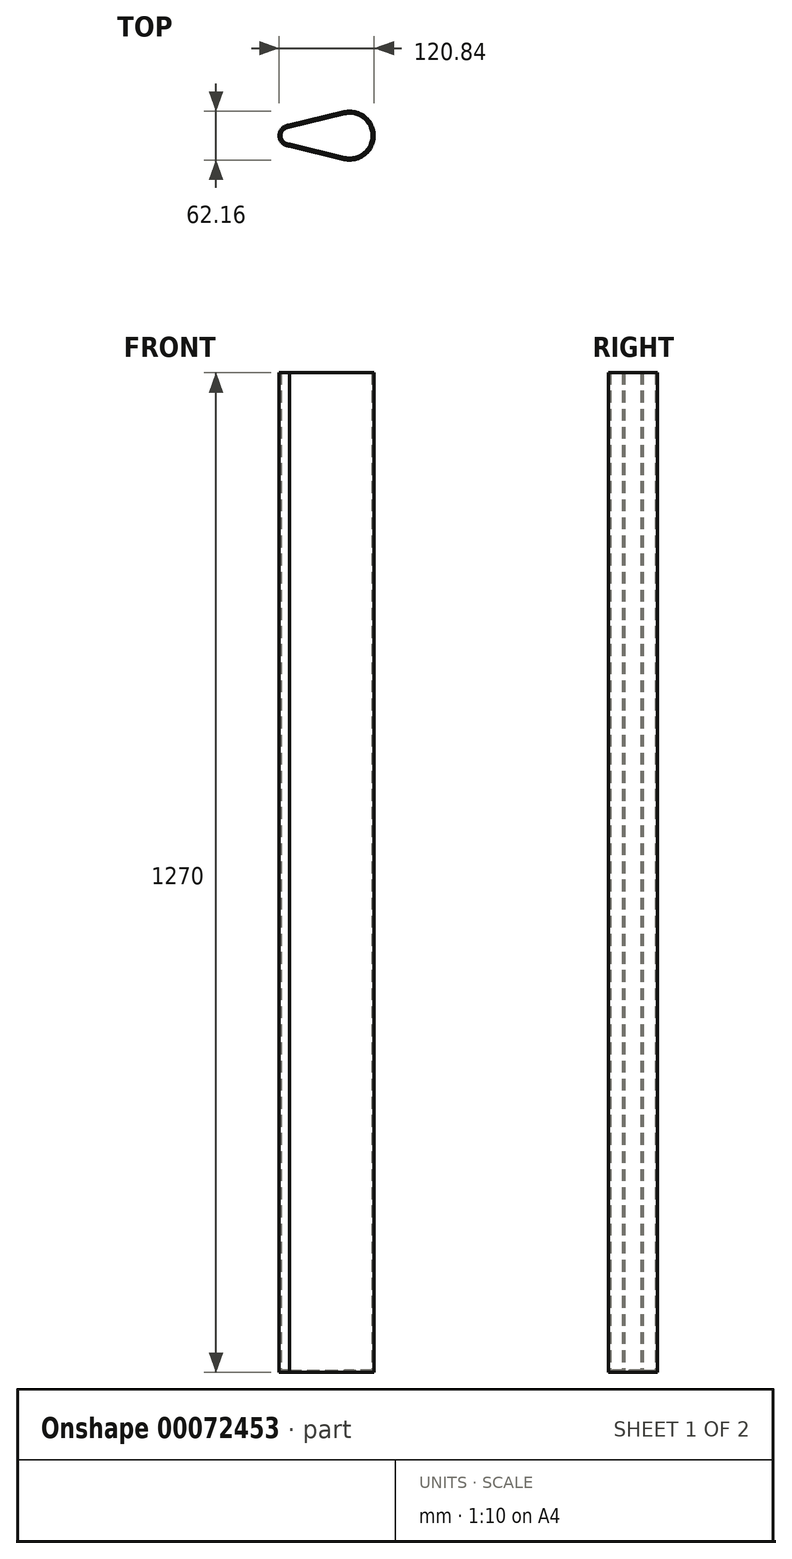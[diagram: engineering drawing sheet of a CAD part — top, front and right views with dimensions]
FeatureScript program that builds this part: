
annotation { "Feature Type Name" : "Feature", "Feature Type Description" : "" }
export const myFeature = defineFeature(function(context is Context, id is Id, definition is map)
    precondition{}
    {
        {
            var Q0;
            Q0=qCreatedBy(makeId("Top.planeOp"),FACE);
            var sketch = newSketch(context, id + "F0", { "sketchPlane" : qUnion([Q0])});
            skArc(sketch, "E0", {"start": v(-7.45, -30.18) * mm, "mid": v(31.08, -0.06) * mm, "end": v(-7.34, 30.2) * mm});
            skArc(sketch, "E1", {"start": v(-77.48, 13.16) * mm, "mid": v(-89.75, -0.6) * mm, "end": v(-76.3, -13.2) * mm});
            skLineSegment(sketch, "E2", {"start": v(-77.48, 13.16) * mm, "end": v(-7.34, 30.2) * mm});
            skLineSegment(sketch, "E3", {"start": v(-76.3, -13.2) * mm, "end": v(-7.45, -30.18) * mm});
            skPoint(sketch, "E4.orphan", {"position": v(0, 31.99) * mm});
            skPoint(sketch, "E5.orphan", {"position": v(0, -32.01) * mm});
            skSolve(sketch);
        }
        {
            var Q0;
            Q0 = qSketchRegion(id + "F0", true);
            extrude(context, id + "F1", {"entities" : qUnion([Q0]), "depth" : 1270 * mm});
        }
        {
            var Q0;
            Q0=makeQuery(id+"F1.opExtrude","CAP_FACE",FACE,{"disambiguationData":[OSD([sQuery(id+"F0.wireOp",EDGE,"E0"),sQuery(id+"F0.wireOp",EDGE,"E1"),sQuery(id+"F0.wireOp",EDGE,"E2"),sQuery(id+"F0.wireOp",EDGE,"E3")])],"isStart":false});
            shell(context, id + "F2", {"entities" : qUnion([Q0]), "thickness" : 2.54 * mm});
        }
    });
